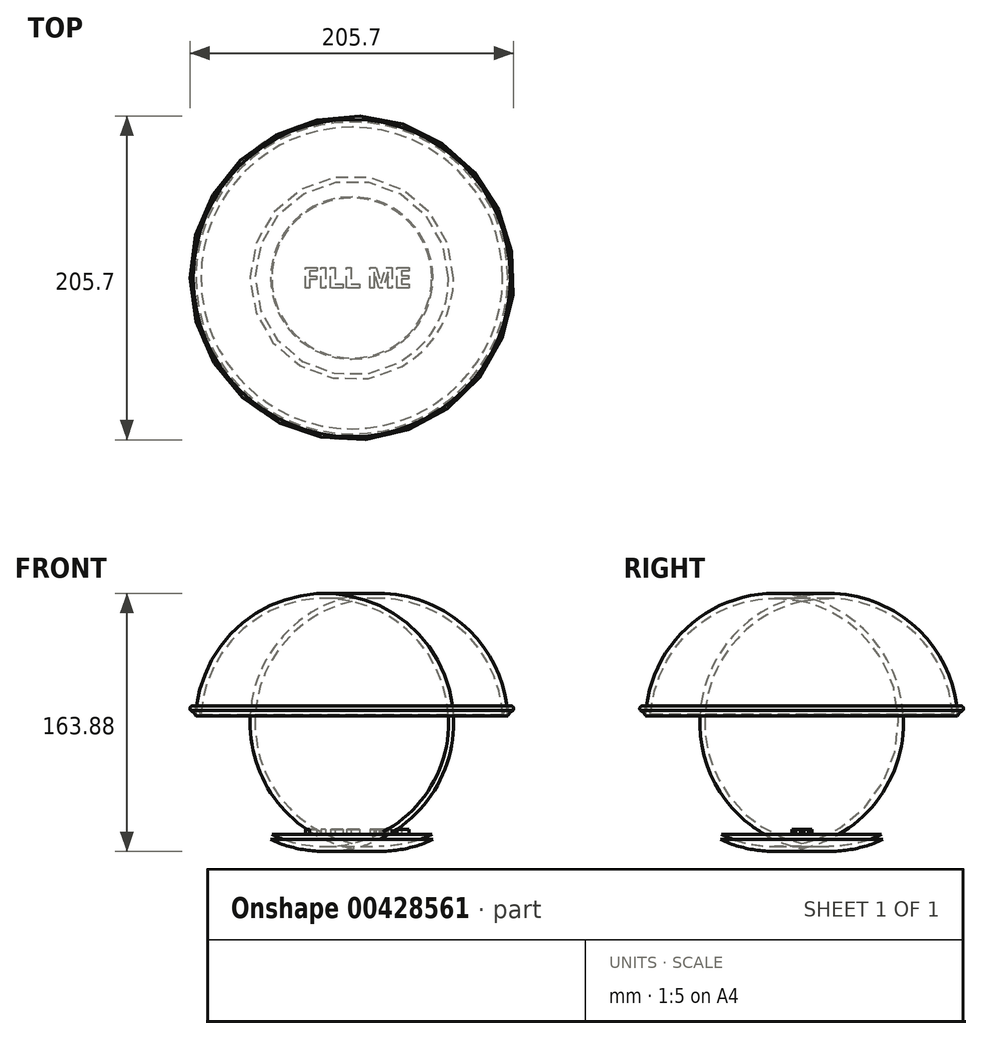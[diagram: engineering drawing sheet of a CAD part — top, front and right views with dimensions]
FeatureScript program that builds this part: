
annotation { "Feature Type Name" : "Feature", "Feature Type Description" : "" }
export const myFeature = defineFeature(function(context is Context, id is Id, definition is map)
    precondition{}
    {
        {
            var Q0;
            Q0=qCreatedBy(makeId("Front.planeOp"),FACE);
            var sketch = newSketch(context, id + "F0", { "sketchPlane" : qUnion([Q0])});
            skArc(sketch, "E0", {"start": v(-45.04, 76.2) * mm, "mid": v(-34.24, 31.18) * mm, "end": v(0, 0) * mm});
            skArc(sketch, "E1", {"start": v(-45.04, 76.2) * mm, "mid": v(-47.1, 79.29) * mm, "end": v(-49.97, 81.64) * mm});
            skLineSegment(sketch, "E2", {"start": v(0, 0) * mm, "end": v(50.8, 0) * mm});
            skArc(sketch, "E3.0", {"start": v(-48.26, 75.51) * mm, "mid": v(-49.71, 77.43) * mm, "end": v(-51.6, 78.92) * mm});
            skArc(sketch, "E3.1", {"start": v(-48.26, 75.51) * mm, "mid": v(-36.56, 28.87) * mm, "end": v(-0.7, -3.18) * mm});
            skLineSegment(sketch, "E3.2", {"start": v(-0.7, -3.18) * mm, "end": v(50.8, -3.18) * mm});
            skArc(sketch, "E4", {"start": v(-49.97, 81.64) * mm, "mid": v(-51.81, 80.9) * mm, "end": v(-51.6, 78.92) * mm});
            skLineSegment(sketch, "E5", {"start": v(50.8, -3.18) * mm, "end": v(50.8, 0) * mm});
            skSolve(sketch);
        }
        {
            var Q0;
            Q0=qSketchRegion(id+"F0",true);
            var Q1;
            Q1=sQuery(id+"F0.wireOp",EDGE,"E5");
            revolve(context, id + "F1", {"entities" : qUnion([Q0]), "axis" : qUnion([Q1]), "revolveType" : RevolveType.FULL});
        }
        {
            var Q0;
            Q0=makeQuery(id+"F1.opRevolve","SWEPT_FACE",FACE,{"disambiguationData":[OSD([sQuery(id+"F0.wireOp",EDGE,"E2")])]});
            var sketch = newSketch(context, id + "F2", { "sketchPlane" : qUnion([Q0])});
            skText(sketch, "E6", { "text": "FILL ME", "fontName": "OpenSans-Bold.ttf"});
            const initialGuessF2  = {"E6": [0.01968, -0.00625, 1, 0, 0.01307]};
            skSetInitialGuess(sketch, initialGuessF2);
            skSolve(sketch);
        }
        {
            var Q0;
            Q0=qSketchRegion(id+"F2",true);
            extrude(context, id + "F3", {"entities" : qUnion([Q0]), "operationType" : NewBodyOperationType.ADD, "depth" : 3.17 * mm});
        }
    });
